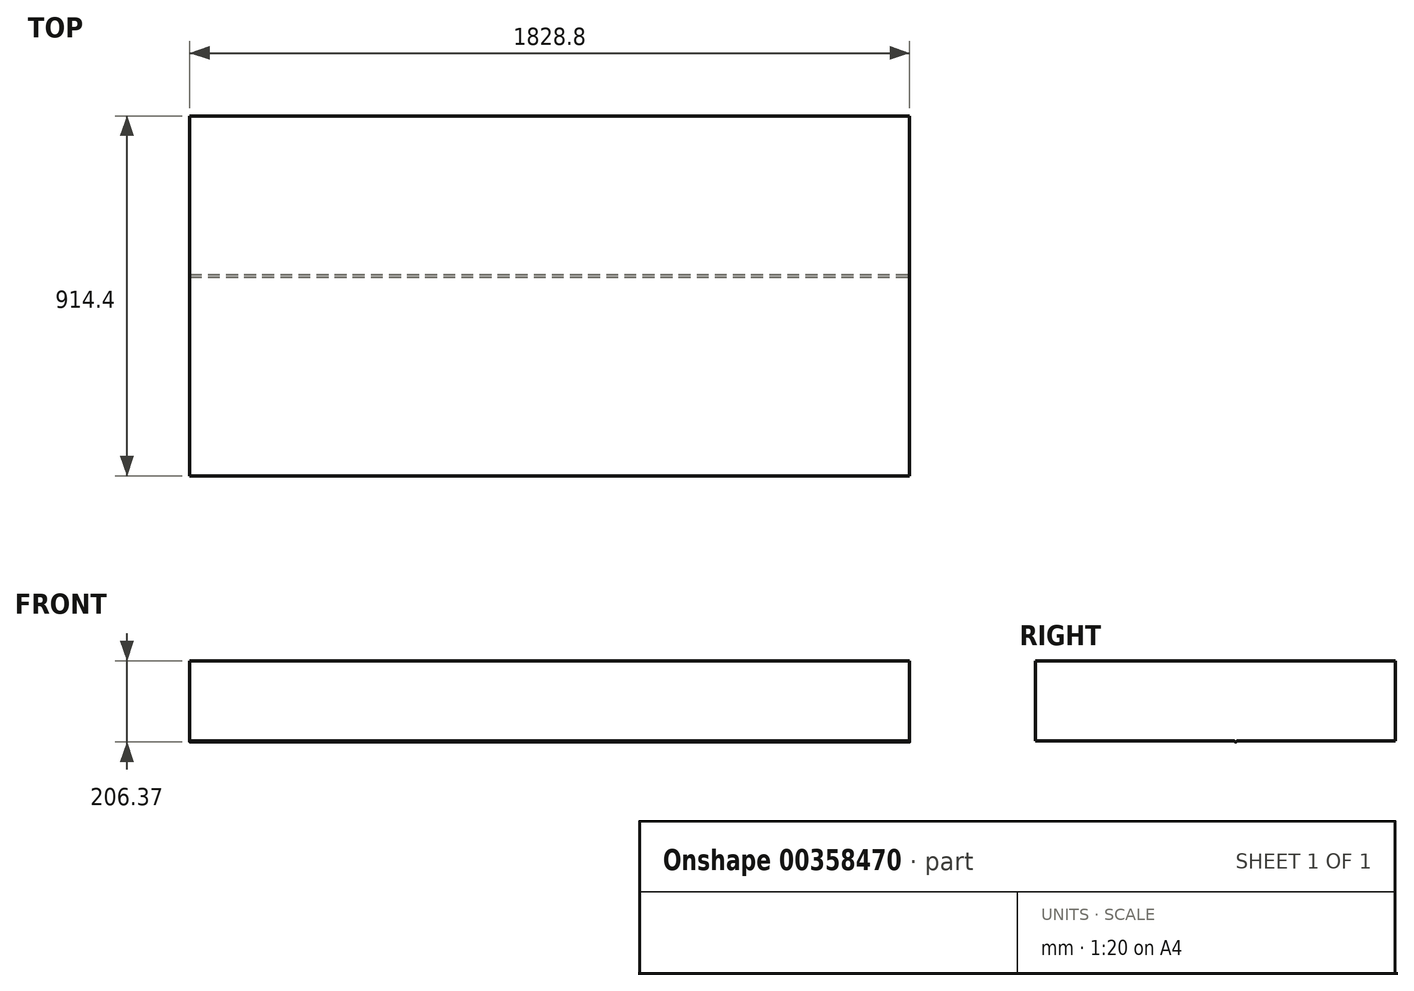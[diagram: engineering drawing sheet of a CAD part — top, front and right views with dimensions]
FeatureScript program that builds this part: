
annotation { "Feature Type Name" : "Feature", "Feature Type Description" : "" }
export const myFeature = defineFeature(function(context is Context, id is Id, definition is map)
    precondition{}
    {
        {
            var Q0;
            Q0=qCreatedBy(makeId("Top.planeOp"),FACE);
            var sketch = newSketch(context, id + "F0", { "sketchPlane" : qUnion([Q0])});
            skLineSegment(sketch, "E0.bottom", {"start": v(1372.59, -418.7) * mm, "end": v(-456.21, -418.7) * mm});
            skLineSegment(sketch, "E0.top", {"start": v(1372.59, 495.7) * mm, "end": v(-456.21, 495.7) * mm});
            skLineSegment(sketch, "E0.left", {"start": v(1372.59, -418.7) * mm, "end": v(1372.59, 495.7) * mm});
            skLineSegment(sketch, "E0.right", {"start": v(-456.21, -418.7) * mm, "end": v(-456.21, 495.7) * mm});
            skSolve(sketch);
        }
        {
            var Q0;
            Q0 = qSketchRegion(id + "F0", true);
            extrude(context, id + "F1", {"entities" : qUnion([Q0]), "depth" : 203.2 * mm});
        }
        {
            var Q0;
            Q0=makeQuery(id+"F1.opExtrude","CAP_FACE",FACE,{"disambiguationData":[OSD([sQuery(id+"F0.wireOp",EDGE,"E0.bottom"),sQuery(id+"F0.wireOp",EDGE,"E0.top"),sQuery(id+"F0.wireOp",EDGE,"E0.left"),sQuery(id+"F0.wireOp",EDGE,"E0.right")])],"isStart":true});
            var sketch = newSketch(context, id + "F2", { "sketchPlane" : qUnion([Q0])});
            skLineSegment(sketch, "E1", {"start": v(1372.59, -89.3) * mm, "end": v(-456.21, -89.3) * mm});
            skSolve(sketch);
        }
        {
            var Q0;
            Q0=makeQuery(id+"F1.opExtrude","SWEPT_FACE",FACE,{"disambiguationData":[OSD([sQuery(id+"F0.wireOp",EDGE,"E0.left")])]});
            var sketch = newSketch(context, id + "F3", { "sketchPlane" : qUnion([Q0])});
            skPoint(sketch, "E2.0", {"position": v(89.3, 0) * mm});
            skCircle(sketch, "E3", {"center": v(89.3, 0) * mm, "radius": 3.18 * mm});
            skSolve(sketch);
        }
        {
            var Q0;
            Q0 = qSketchRegion(id + "F3", true);
            extrude(context, id + "F4", {"entities" : qUnion([Q0]), "operationType" : NewBodyOperationType.ADD, "oppositeDirection" : true, "depth" : 1828.8 * mm});
        }
    });
